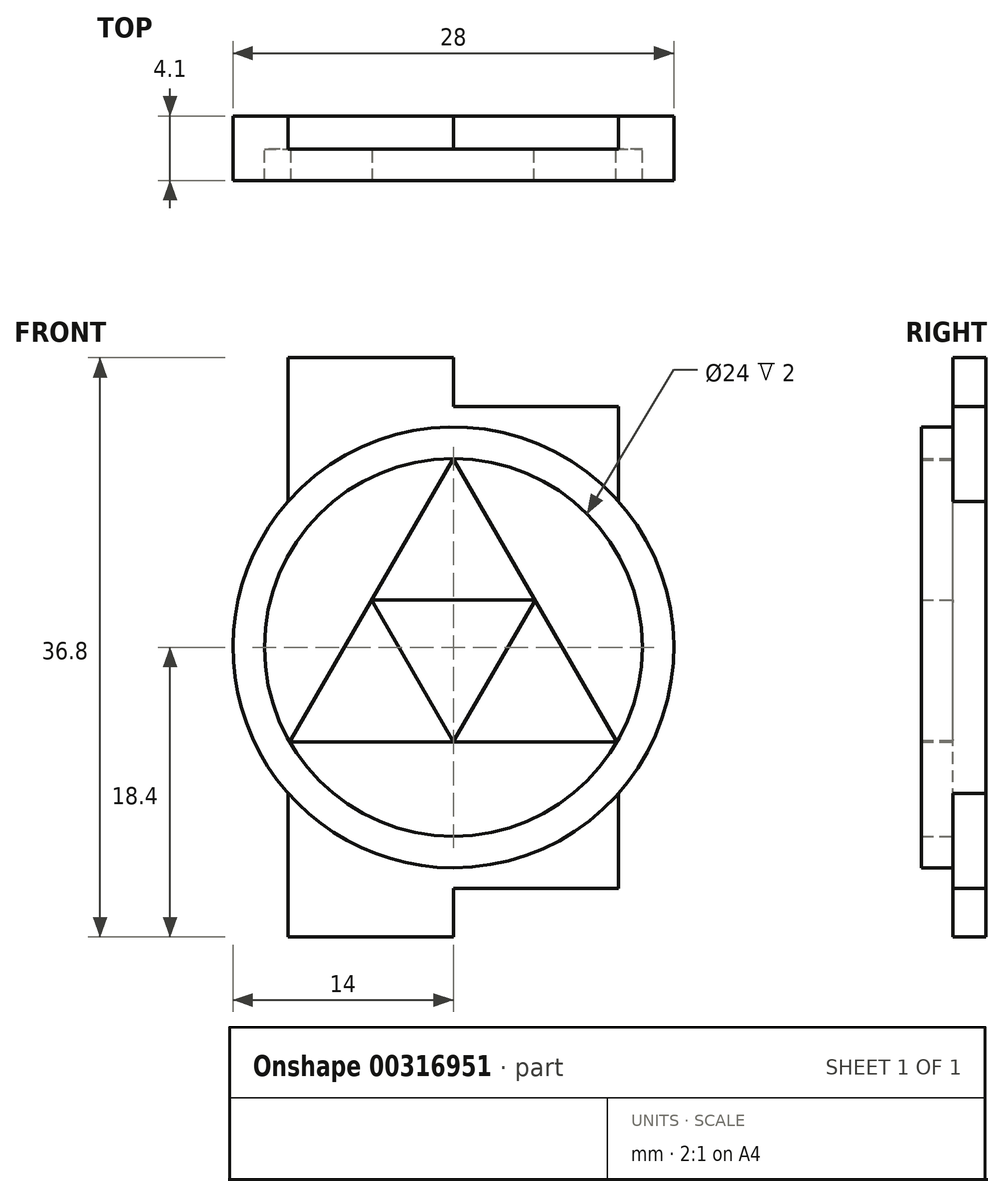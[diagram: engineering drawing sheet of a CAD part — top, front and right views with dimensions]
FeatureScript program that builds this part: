
annotation { "Feature Type Name" : "Feature", "Feature Type Description" : "" }
export const myFeature = defineFeature(function(context is Context, id is Id, definition is map)
    precondition{}
    {
        {
            var Q0;
            Q0=qCreatedBy(makeId("Front.planeOp"),FACE);
            var sketch = newSketch(context, id + "F0", { "sketchPlane" : qUnion([Q0])});
            skArc(sketch, "E0", {"start": v(-14, 0) * mm, "mid": v(-13.1, -4.95) * mm, "end": v(-10.5, -9.26) * mm});
            skLineSegment(sketch, "E1", {"start": v(0, 0) * mm, "end": v(-10.5, 0) * mm, "construction": true});
            skLineSegment(sketch, "E2.MirrorCS", {"start": v(0, 0) * mm, "end": v(10.5, 0) * mm, "construction": true});
            skLineSegment(sketch, "E3", {"start": v(-10.5, -9.26) * mm, "end": v(-10.5, -18.4) * mm});
            skLineSegment(sketch, "E4", {"start": v(-10.5, -18.4) * mm, "end": v(0, -18.4) * mm});
            skLineSegment(sketch, "E5", {"start": v(0, -18.4) * mm, "end": v(0, -15.3) * mm});
            skLineSegment(sketch, "E6", {"start": v(0, -15.3) * mm, "end": v(10.5, -15.3) * mm});
            skLineSegment(sketch, "E7", {"start": v(10.5, -15.3) * mm, "end": v(10.5, -9.26) * mm});
            skLineSegment(sketch, "E8", {"start": v(-14, 0) * mm, "end": v(14, 0) * mm, "construction": true});
            skArc(sketch, "E9.MirrorCS", {"start": v(-14, 0) * mm, "mid": v(-13.1, 4.95) * mm, "end": v(-10.5, 9.26) * mm});
            skLineSegment(sketch, "E10.MirrorCS", {"start": v(-10.5, 9.26) * mm, "end": v(-10.5, 18.4) * mm});
            skLineSegment(sketch, "E11.MirrorCS", {"start": v(0, 15.3) * mm, "end": v(10.5, 15.3) * mm});
            skLineSegment(sketch, "E12.MirrorCS", {"start": v(-10.5, 18.4) * mm, "end": v(0, 18.4) * mm});
            skLineSegment(sketch, "E13.MirrorCS", {"start": v(10.5, 15.3) * mm, "end": v(10.5, 9.26) * mm});
            skLineSegment(sketch, "E14.MirrorCS", {"start": v(0, 18.4) * mm, "end": v(0, 15.3) * mm});
            skArc(sketch, "E15.trimOffspring", {"start": v(10.5, 9.26) * mm, "mid": v(13.1, 4.95) * mm, "end": v(14, 0) * mm});
            skArc(sketch, "E16.trimOffspring", {"start": v(10.5, -9.26) * mm, "mid": v(13.1, -4.95) * mm, "end": v(14, 0) * mm});
            skSolve(sketch);
        }
        {
            var Q0;
            Q0=makeQuery(id+"F0.imprint","IMPRINT",FACE,{"disambiguationData":[TD([[makeQuery(id+"F0.imprint","IMPRINT",EDGE,{"derivedFrom":sQuery(id+"F0.wireOp",EDGE,"E0")}),1.0]])]});
            extrude(context, id + "F1", {"entities" : qUnion([Q0]), "depth" : 2.1 * mm});
        }
        {
            var Q0;
            Q0=makeQuery(id+"F1.opExtrude","CAP_FACE",FACE,{"disambiguationData":[OSD([sQuery(id+"F0.wireOp",EDGE,"E0"),sQuery(id+"F0.wireOp",EDGE,"E3"),sQuery(id+"F0.wireOp",EDGE,"E4"),sQuery(id+"F0.wireOp",EDGE,"E5"),sQuery(id+"F0.wireOp",EDGE,"E6"),sQuery(id+"F0.wireOp",EDGE,"E7"),sQuery(id+"F0.wireOp",EDGE,"E9.MirrorCS"),sQuery(id+"F0.wireOp",EDGE,"E10.MirrorCS"),sQuery(id+"F0.wireOp",EDGE,"E11.MirrorCS"),sQuery(id+"F0.wireOp",EDGE,"E12.MirrorCS"),sQuery(id+"F0.wireOp",EDGE,"E13.MirrorCS"),sQuery(id+"F0.wireOp",EDGE,"E14.MirrorCS"),sQuery(id+"F0.wireOp",EDGE,"E15.trimOffspring"),sQuery(id+"F0.wireOp",EDGE,"E16.trimOffspring")])],"isStart":false});
            var sketch = newSketch(context, id + "F2", { "sketchPlane" : qUnion([Q0])});
            skCircle(sketch, "E17", {"center": v(0, 0) * mm, "radius": 14 * mm});
            skCircle(sketch, "E18", {"center": v(0, 0) * mm, "radius": 12 * mm});
            skCircle(sketch, "E19.cCircle", {"center": v(0, 0) * mm, "radius": 12 * mm, "construction": true});
            skLineSegment(sketch, "E19.0", {"start": v(0.09, 11.85) * mm, "end": v(10.3, -5.85) * mm});
            skLineSegment(sketch, "E19.1", {"start": v(10.22, -6) * mm, "end": v(-10.22, -6) * mm});
            skLineSegment(sketch, "E19.2", {"start": v(-10.3, -5.85) * mm, "end": v(-0.09, 11.85) * mm});
            skPoint(sketch, "E20.visualSharp", {"position": v(-10.4, -6) * mm});
            skArc(sketch, "E20.filletArc", {"start": v(-10.3, -5.85) * mm, "mid": v(-10.3, -5.95) * mm, "end": v(-10.22, -6) * mm});
            skPoint(sketch, "E21.visualSharp", {"position": v(0, 12) * mm});
            skArc(sketch, "E21.filletArc", {"start": v(0.09, 11.85) * mm, "mid": v(0, 11.9) * mm, "end": v(-0.09, 11.85) * mm});
            skPoint(sketch, "E22.visualSharp", {"position": v(10.4, -6) * mm});
            skArc(sketch, "E22.filletArc", {"start": v(10.22, -6) * mm, "mid": v(10.3, -5.95) * mm, "end": v(10.3, -5.85) * mm});
            skCircle(sketch, "E23.cCircle", {"center": v(0, 0) * mm, "radius": 6 * mm, "construction": true});
            skLineSegment(sketch, "E23.0", {"start": v(-0.09, -5.85) * mm, "end": v(-5.1, 2.85) * mm});
            skLineSegment(sketch, "E23.1", {"start": v(-5.02, 3) * mm, "end": v(5.02, 3) * mm});
            skLineSegment(sketch, "E23.2", {"start": v(5.1, 2.85) * mm, "end": v(0.09, -5.85) * mm});
            skPoint(sketch, "E24.visualSharp", {"position": v(-5.2, 3) * mm});
            skArc(sketch, "E24.filletArc", {"start": v(-5.02, 3) * mm, "mid": v(-5.1, 2.95) * mm, "end": v(-5.1, 2.85) * mm});
            skPoint(sketch, "E25.visualSharp", {"position": v(0, -6) * mm});
            skArc(sketch, "E25.filletArc", {"start": v(-0.09, -5.85) * mm, "mid": v(0, -5.9) * mm, "end": v(0.09, -5.85) * mm});
            skPoint(sketch, "E26.visualSharp", {"position": v(5.2, 3) * mm});
            skArc(sketch, "E26.filletArc", {"start": v(5.1, 2.85) * mm, "mid": v(5.1, 2.95) * mm, "end": v(5.02, 3) * mm});
            skSolve(sketch);
        }
        {
            var Q0;
            Q0=makeQuery(id+"F2.imprint","IMPRINT",FACE,{"disambiguationData":[TD([[makeQuery(id+"F2.imprint","IMPRINT",EDGE,{"derivedFrom":sQuery(id+"F2.wireOp",EDGE,"E18")}),-1.0]])]});
            var Q1;
            Q1=makeQuery(id+"F2.imprint","IMPRINT",FACE,{"disambiguationData":[TD([[makeQuery(id+"F2.imprint","IMPRINT",EDGE,{"derivedFrom":sQuery(id+"F2.wireOp",EDGE,"E19.0")}),-1.0]])]});
            extrude(context, id + "F3", {"entities" : qUnion([Q0, Q1]), "operationType" : NewBodyOperationType.ADD, "depth" : 2 * mm});
        }
    });
